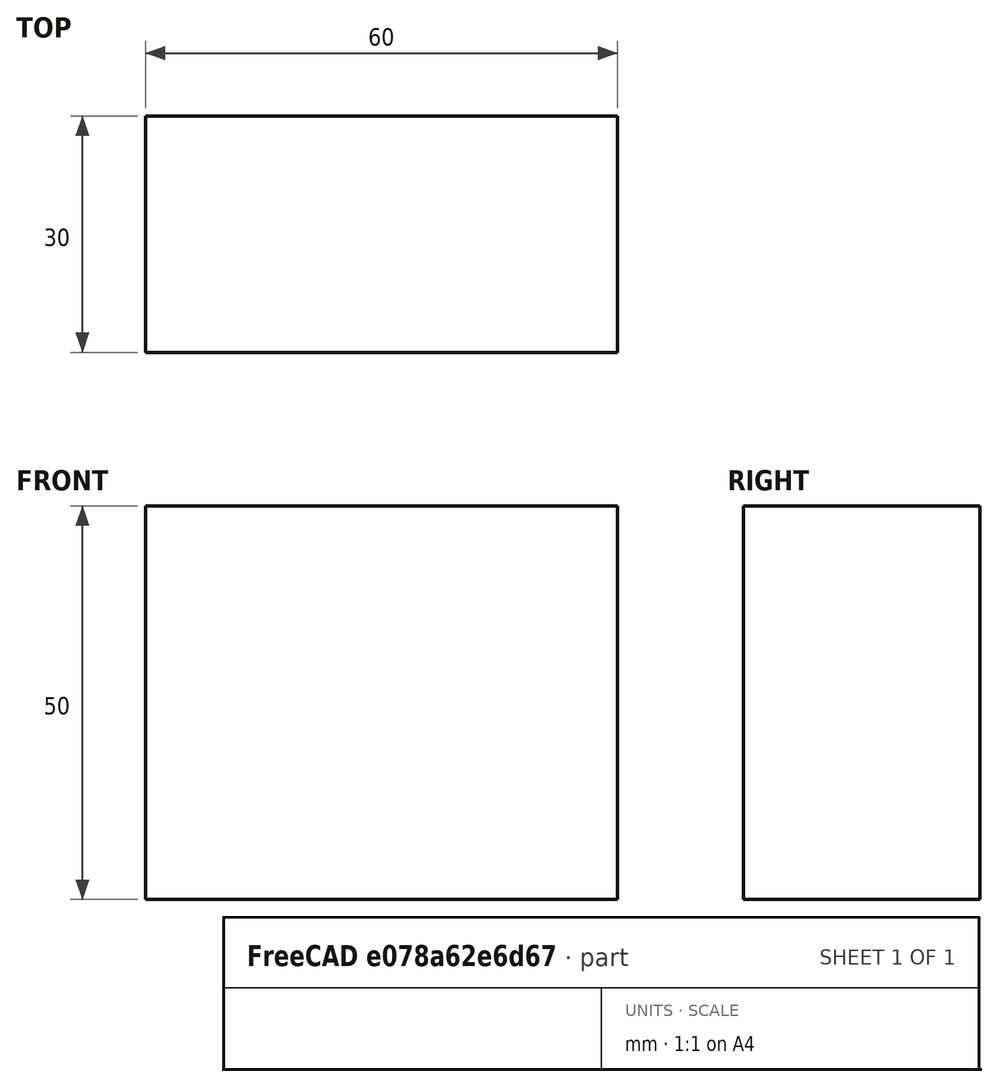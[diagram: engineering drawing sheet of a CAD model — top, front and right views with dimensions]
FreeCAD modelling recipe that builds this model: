
FCSTD DOCUMENT  (FreeCAD 0.15R4671 (Git))
Label: Flat Bar 60x30 EN10058 S235JR
License: All rights reserved
LicenseURL: http://en.wikipedia.org/wiki/All_rights_reserved
objects: Sketcher::SketchObject×1, Part::Extrusion×1
note: 2 computed .brp shape members not serialized (recipe doc carries the construction recipe); baked Part::Feature solids carry a one-line shape summary decoded from their .brp

FEATURE [Sketcher::SketchObject] Sketch
  sketch-geometry (4):
    g0: LineSegment StartX=-30 StartY=-15 StartZ=0 EndX=30 EndY=-15 EndZ=0
    g1: LineSegment StartX=30 StartY=-15 StartZ=0 EndX=30 EndY=15 EndZ=0
    g2: LineSegment StartX=30 StartY=15 StartZ=0 EndX=-30 EndY=15 EndZ=0
    g3: LineSegment StartX=-30 StartY=15 StartZ=0 EndX=-30 EndY=-15 EndZ=0
  constraints (12):
    c: Coincident(g0,g1)
    c: Coincident(g1,g2)
    c: Coincident(g2,g3)
    c: Coincident(g3,g0)
    c: Horizontal(g0)
    c: Horizontal(g2)
    c: Vertical(g1)
    c: Vertical(g3)
    c: Symmetric(g1,g2,g-2)
    c: Symmetric(g0,g1,g-1)
    c: DistanceY(g1) = 30
    c: DistanceX(g0) = 60
FEATURE [Part::Extrusion] Extrude  label="Flat Bar 60x30 EN10058 S235JR"
  Base = -> Sketch
  Dir = (0,0,50)
  Solid = true
